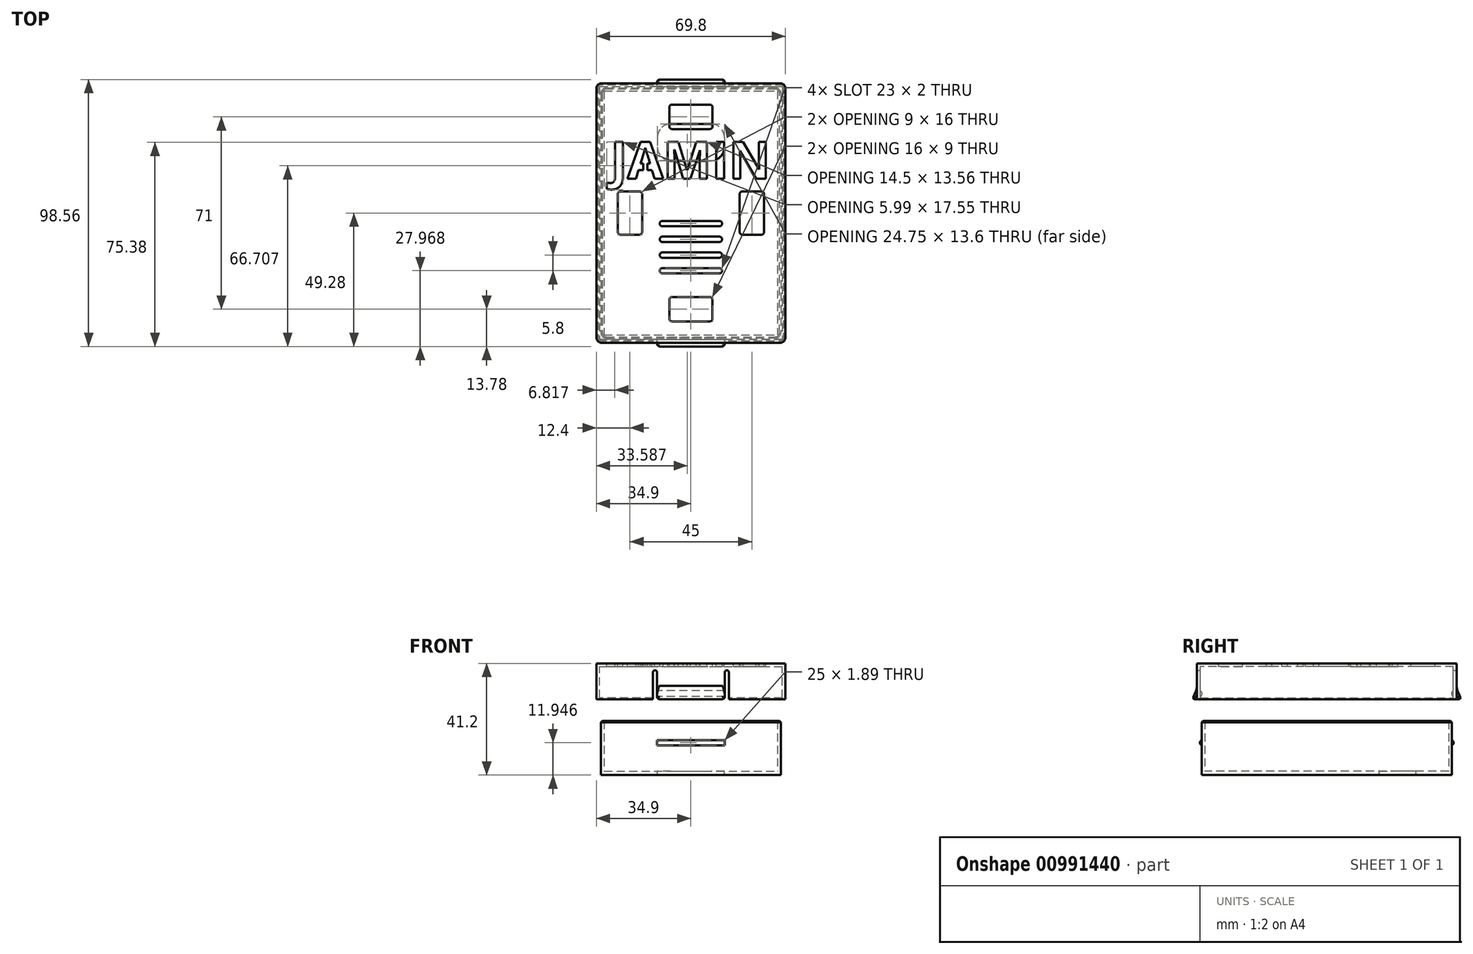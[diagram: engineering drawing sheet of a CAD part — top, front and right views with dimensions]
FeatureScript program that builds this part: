
annotation { "Feature Type Name" : "Feature", "Feature Type Description" : "" }
export const myFeature = defineFeature(function(context is Context, id is Id, definition is map)
    precondition{}
    {
        {
            var Q0;
            Q0=qCreatedBy(makeId("Top.planeOp"),FACE);
            var sketch = newSketch(context, id + "F0", { "sketchPlane" : qUnion([Q0])});
            skLineSegment(sketch, "E0.bottom", {"start": v(-32, 45) * mm, "end": v(32, 45) * mm});
            skLineSegment(sketch, "E0.top", {"start": v(-32, -45) * mm, "end": v(32, -45) * mm});
            skLineSegment(sketch, "E0.left", {"start": v(-32, 45) * mm, "end": v(-32, -45) * mm});
            skLineSegment(sketch, "E0.right", {"start": v(32, 45) * mm, "end": v(32, -45) * mm});
            skLineSegment(sketch, "E1.0", {"start": v(-33.2, 46.2) * mm, "end": v(-33.2, -46.2) * mm});
            skLineSegment(sketch, "E1.1", {"start": v(-33.2, 46.2) * mm, "end": v(33.2, 46.2) * mm});
            skLineSegment(sketch, "E1.2", {"start": v(33.2, 46.2) * mm, "end": v(33.2, -46.2) * mm});
            skLineSegment(sketch, "E1.3", {"start": v(-33.2, -46.2) * mm, "end": v(33.2, -46.2) * mm});
            skSolve(sketch);
        }
        {
            var Q0;
            Q0=makeQuery(id+"F0.imprint","IMPRINT",FACE,{"disambiguationData":[TD([[makeQuery(id+"F0.imprint","IMPRINT",EDGE,{"derivedFrom":sQuery(id+"F0.wireOp",EDGE,"E0.bottom")}),-1.0]])]});
            extrude(context, id + "F1", {"entities" : qUnion([Q0]), "depth" : 1.4 * mm, "offsetDistance" : 25 * mm});
        }
        {
            var Q0;
            Q0=makeQuery(id+"F0.imprint","IMPRINT",FACE,{"disambiguationData":[TD([[makeQuery(id+"F0.imprint","IMPRINT",EDGE,{"derivedFrom":sQuery(id+"F0.wireOp",EDGE,"E0.bottom")}),1.0]])]});
            extrude(context, id + "F2", {"entities" : qUnion([Q0]), "operationType" : NewBodyOperationType.ADD, "depth" : 20 * mm, "offsetDistance" : 25 * mm});
        }
        {
            var Q0;
            Q0=makeQuery(id+"F1.opExtrude","CAP_FACE",FACE,{"disambiguationData":[OSD([sQuery(id+"F0.wireOp",EDGE,"E0.bottom"),sQuery(id+"F0.wireOp",EDGE,"E0.top"),sQuery(id+"F0.wireOp",EDGE,"E0.left"),sQuery(id+"F0.wireOp",EDGE,"E0.right")])],"isStart":false});
            var sketch = newSketch(context, id + "F3", { "sketchPlane" : qUnion([Q0])});
            skLineSegment(sketch, "E2.bottom", {"start": v(-12.38, 32.9) * mm, "end": v(12.38, 32.9) * mm});
            skLineSegment(sketch, "E2.top", {"start": v(-12.38, 19.3) * mm, "end": v(12.38, 19.3) * mm});
            skLineSegment(sketch, "E2.left", {"start": v(-12.38, 32.9) * mm, "end": v(-12.38, 19.3) * mm});
            skLineSegment(sketch, "E2.right", {"start": v(12.38, 32.9) * mm, "end": v(12.38, 19.3) * mm});
            skSolve(sketch);
        }
        {
            var Q0;
            Q0=makeQuery(id+"F3.imprint","IMPRINT",FACE,{"disambiguationData":[TD([[makeQuery(id+"F3.imprint","IMPRINT",EDGE,{"derivedFrom":sQuery(id+"F3.wireOp",EDGE,"E2.bottom")}),-1.0]])]});
            extrude(context, id + "F4", {"entities" : qUnion([Q0]), "operationType" : NewBodyOperationType.REMOVE, "oppositeDirection" : true, "depth" : 25 * mm, "offsetDistance" : 25 * mm});
        }
        {
            var Q0;
            Q0=makeQuery(id+"F4.boolean.opBoolean","COPY",EDGE,{"derivedFrom":makeQuery(id+"F4.opExtrude","SWEPT_EDGE",EDGE,{"disambiguationData":[OSD([sQuery(id+"F3.wireOp",EDGE,"E2.bottom"),sQuery(id+"F3.wireOp",EDGE,"E2.left")])]})});
            var Q1;
            Q1=makeQuery(id+"F4.boolean.opBoolean","COPY",EDGE,{"derivedFrom":makeQuery(id+"F4.opExtrude","SWEPT_EDGE",EDGE,{"disambiguationData":[OSD([sQuery(id+"F3.wireOp",EDGE,"E2.top"),sQuery(id+"F3.wireOp",EDGE,"E2.right")])]})});
            var Q2;
            Q2=makeQuery(id+"F4.boolean.opBoolean","COPY",EDGE,{"derivedFrom":makeQuery(id+"F4.opExtrude","SWEPT_EDGE",EDGE,{"disambiguationData":[OSD([sQuery(id+"F3.wireOp",EDGE,"E2.bottom"),sQuery(id+"F3.wireOp",EDGE,"E2.right")])]})});
            var Q3;
            Q3=makeQuery(id+"F4.boolean.opBoolean","COPY",EDGE,{"derivedFrom":makeQuery(id+"F4.opExtrude","SWEPT_EDGE",EDGE,{"disambiguationData":[OSD([sQuery(id+"F3.wireOp",EDGE,"E2.top"),sQuery(id+"F3.wireOp",EDGE,"E2.left")])]})});
            fillet(context, id + "F5", {"entities" : qUnion([Q0, Q1, Q2, Q3]), "radius" : 5 * mm, "tangentPropagation" : true, "allowEdgeOverflow" : false});
        }
        {
            var Q0;
            Q0=makeQuery(id+"F2.opExtrude","SWEPT_EDGE",EDGE,{"disambiguationData":[OSD([sQuery(id+"F0.wireOp",EDGE,"E1.2"),sQuery(id+"F0.wireOp",EDGE,"E1.3")])]});
            var Q1;
            Q1=makeQuery(id+"F2.opExtrude","SWEPT_EDGE",EDGE,{"disambiguationData":[OSD([sQuery(id+"F0.wireOp",EDGE,"E1.1"),sQuery(id+"F0.wireOp",EDGE,"E1.2")])]});
            var Q2;
            Q2=makeQuery(id+"F2.opExtrude","SWEPT_EDGE",EDGE,{"disambiguationData":[OSD([sQuery(id+"F0.wireOp",EDGE,"E1.0"),sQuery(id+"F0.wireOp",EDGE,"E1.1")])]});
            var Q3;
            Q3=makeQuery(id+"F2.opExtrude","SWEPT_EDGE",EDGE,{"disambiguationData":[OSD([sQuery(id+"F0.wireOp",EDGE,"E1.0"),sQuery(id+"F0.wireOp",EDGE,"E1.3")])]});
            fillet(context, id + "F6", {"entities" : qUnion([Q0, Q1, Q2, Q3]), "radius" : 2 * mm, "tangentPropagation" : true, "allowEdgeOverflow" : false});
        }
        {
            var Q0;
            Q0=qCreatedBy(makeId("Right.planeOp"),FACE);
            var sketch = newSketch(context, id + "F7", { "sketchPlane" : qUnion([Q0])});
            skArc(sketch, "E3", {"start": v(-46.2, 12.9) * mm, "mid": v(-46.81, 11.95) * mm, "end": v(-46.2, 11) * mm});
            skLineSegment(sketch, "E4", {"start": v(-46.2, 12.9) * mm, "end": v(-46.2, 11) * mm});
            skSolve(sketch);
        }
        {
            var Q0;
            Q0=makeQuery(id+"F7.imprint","IMPRINT",FACE,{"disambiguationData":[TD([[makeQuery(id+"F7.imprint","IMPRINT",EDGE,{"derivedFrom":sQuery(id+"F7.wireOp",EDGE,"E3")}),1.0]])]});
            extrude(context, id + "F8", {"entities" : qUnion([Q0]), "endBound" : BoundingType.SYMMETRIC, "depth" : 25 * mm, "offsetDistance" : 25 * mm});
        }
        {
            var Q0;
            Q0=makeQuery(id+"F8.opExtrude","SWEPT_BODY",BODY,{"disambiguationData":[OSD([sQuery(id+"F7.wireOp",EDGE,"E3"),sQuery(id+"F7.wireOp",EDGE,"E4")])]});
            var Q1;
            Q1=qCreatedBy(makeId("Front.planeOp"),FACE);
            mirror(context, id + "F9", {"operationType" : NewBodyOperationType.ADD, "entities" : qUnion([Q0]), "mirrorPlane" : qUnion([Q1])});
        }
        {
            var Q0;
            Q0=qCreatedBy(makeId("Top.planeOp"),FACE);
            cPlane(context, id + "F10", {"entities" : qUnion([Q0]), "cplaneType" : CPlaneType.OFFSET, "offset" : 40 * mm, "width" : 150 * mm, "height" : 150 * mm});
        }
        {
            var Q0;
            Q0=qCreatedBy(id+"F10.planeOp",FACE);
            var sketch = newSketch(context, id + "F11", { "sketchPlane" : qUnion([Q0])});
            skLineSegment(sketch, "E5.bottom", {"start": v(-33.7, 46.7) * mm, "end": v(33.7, 46.7) * mm});
            skLineSegment(sketch, "E5.top", {"start": v(-33.7, -46.7) * mm, "end": v(33.7, -46.7) * mm});
            skLineSegment(sketch, "E5.left", {"start": v(-33.7, 46.7) * mm, "end": v(-33.7, -46.7) * mm});
            skLineSegment(sketch, "E5.right", {"start": v(33.7, 46.7) * mm, "end": v(33.7, -46.7) * mm});
            skLineSegment(sketch, "E6.0", {"start": v(-34.9, 47.9) * mm, "end": v(-34.9, -47.9) * mm});
            skLineSegment(sketch, "E6.1", {"start": v(-34.9, 47.9) * mm, "end": v(34.9, 47.9) * mm});
            skLineSegment(sketch, "E6.2", {"start": v(34.9, 47.9) * mm, "end": v(34.9, -47.9) * mm});
            skLineSegment(sketch, "E6.3", {"start": v(-34.9, -47.9) * mm, "end": v(34.9, -47.9) * mm});
            skSolve(sketch);
        }
        {
            var Q0;
            Q0=makeQuery(id+"F11.imprint","IMPRINT",FACE,{"disambiguationData":[TD([[makeQuery(id+"F11.imprint","IMPRINT",EDGE,{"derivedFrom":sQuery(id+"F11.wireOp",EDGE,"E5.bottom")}),1.0]])]});
            extrude(context, id + "F12", {"entities" : qUnion([Q0]), "operationType" : NewBodyOperationType.ADD, "oppositeDirection" : true, "depth" : 12 * mm, "offsetDistance" : 25 * mm});
        }
        {
            var Q0;
            Q0=qCreatedBy(makeId("Right.planeOp"),FACE);
            var sketch = newSketch(context, id + "F13", { "sketchPlane" : qUnion([Q0])});
            skArc(sketch, "E7", {"start": v(46.7, 31.15) * mm, "mid": v(46.03, 30.07) * mm, "end": v(46.7, 29) * mm});
            skLineSegment(sketch, "E8", {"start": v(46.7, 31.15) * mm, "end": v(46.7, 29) * mm});
            skSolve(sketch);
        }
        {
            var Q0;
            Q0=makeQuery(id+"F13.imprint","IMPRINT",FACE,{"disambiguationData":[TD([[makeQuery(id+"F13.imprint","IMPRINT",EDGE,{"derivedFrom":sQuery(id+"F13.wireOp",EDGE,"E7")}),1.0]])]});
            extrude(context, id + "F14", {"entities" : qUnion([Q0]), "endBound" : BoundingType.SYMMETRIC, "depth" : 25 * mm, "offsetDistance" : 25 * mm});
        }
        {
            var Q0;
            Q0=makeQuery(id+"F14.opExtrude","SWEPT_BODY",BODY,{"disambiguationData":[OSD([sQuery(id+"F13.wireOp",EDGE,"E7"),sQuery(id+"F13.wireOp",EDGE,"E8")])]});
            var Q1;
            Q1=qCreatedBy(makeId("Front.planeOp"),FACE);
            mirror(context, id + "F15", {"operationType" : NewBodyOperationType.ADD, "entities" : qUnion([Q0]), "mirrorPlane" : qUnion([Q1])});
        }
        {
            var Q0;
            Q0=makeQuery(id+"F12.opExtrude","CAP_FACE",FACE,{"disambiguationData":[OSD([sQuery(id+"F11.wireOp",EDGE,"E5.bottom"),sQuery(id+"F11.wireOp",EDGE,"E5.top"),sQuery(id+"F11.wireOp",EDGE,"E5.left"),sQuery(id+"F11.wireOp",EDGE,"E5.right"),sQuery(id+"F11.wireOp",EDGE,"E6.0"),sQuery(id+"F11.wireOp",EDGE,"E6.1"),sQuery(id+"F11.wireOp",EDGE,"E6.2"),sQuery(id+"F11.wireOp",EDGE,"E6.3")])],"isStart":true});
            var sketch = newSketch(context, id + "F16", { "sketchPlane" : qUnion([Q0])});
            skLineSegment(sketch, "E9.bottom", {"start": v(-34.9, 47.9) * mm, "end": v(34.9, 47.9) * mm});
            skLineSegment(sketch, "E9.top", {"start": v(-34.9, -47.9) * mm, "end": v(34.9, -47.9) * mm});
            skLineSegment(sketch, "E9.left", {"start": v(-34.9, 47.9) * mm, "end": v(-34.9, -47.9) * mm});
            skLineSegment(sketch, "E9.right", {"start": v(34.9, 47.9) * mm, "end": v(34.9, -47.9) * mm});
            skSolve(sketch);
        }
        {
            var Q0;
            Q0 = qSketchRegion(id + "F16", true);
            extrude(context, id + "F17", {"entities" : qUnion([Q0]), "operationType" : NewBodyOperationType.ADD, "depth" : 1.2 * mm, "offsetDistance" : 25 * mm});
        }
        {
            var Q0;
            Q0=makeQuery(id+"F17.boolean.opBoolean","MERGE",EDGE,{"derivedFrom":[makeQuery(id+"F12.opExtrude","SWEPT_EDGE",EDGE,{"disambiguationData":[OSD([sQuery(id+"F11.wireOp",EDGE,"E6.1"),sQuery(id+"F11.wireOp",EDGE,"E6.2")])]}),makeQuery(id+"F17.opExtrude","SWEPT_EDGE",EDGE,{"disambiguationData":[OSD([sQuery(id+"F16.wireOp",EDGE,"E9.bottom"),sQuery(id+"F16.wireOp",EDGE,"E9.right")])]})]});
            var Q1;
            Q1=makeQuery(id+"F17.boolean.opBoolean","MERGE",EDGE,{"derivedFrom":[makeQuery(id+"F12.opExtrude","SWEPT_EDGE",EDGE,{"disambiguationData":[OSD([sQuery(id+"F11.wireOp",EDGE,"E6.0"),sQuery(id+"F11.wireOp",EDGE,"E6.1")])]}),makeQuery(id+"F17.opExtrude","SWEPT_EDGE",EDGE,{"disambiguationData":[OSD([sQuery(id+"F16.wireOp",EDGE,"E9.bottom"),sQuery(id+"F16.wireOp",EDGE,"E9.left")])]})]});
            var Q2;
            Q2=makeQuery(id+"F17.boolean.opBoolean","MERGE",EDGE,{"derivedFrom":[makeQuery(id+"F12.opExtrude","SWEPT_EDGE",EDGE,{"disambiguationData":[OSD([sQuery(id+"F11.wireOp",EDGE,"E6.0"),sQuery(id+"F11.wireOp",EDGE,"E6.3")])]}),makeQuery(id+"F17.opExtrude","SWEPT_EDGE",EDGE,{"disambiguationData":[OSD([sQuery(id+"F16.wireOp",EDGE,"E9.top"),sQuery(id+"F16.wireOp",EDGE,"E9.left")])]})]});
            var Q3;
            Q3=makeQuery(id+"F17.boolean.opBoolean","MERGE",EDGE,{"derivedFrom":[makeQuery(id+"F12.opExtrude","SWEPT_EDGE",EDGE,{"disambiguationData":[OSD([sQuery(id+"F11.wireOp",EDGE,"E6.2"),sQuery(id+"F11.wireOp",EDGE,"E6.3")])]}),makeQuery(id+"F17.opExtrude","SWEPT_EDGE",EDGE,{"disambiguationData":[OSD([sQuery(id+"F16.wireOp",EDGE,"E9.top"),sQuery(id+"F16.wireOp",EDGE,"E9.right")])]})]});
            fillet(context, id + "F18", {"entities" : qUnion([Q0, Q1, Q2, Q3]), "radius" : 2 * mm, "tangentPropagation" : true, "allowEdgeOverflow" : false});
        }
        {
            var Q0;
            Q0=qCreatedBy(makeId("Front.planeOp"),FACE);
            var sketch = newSketch(context, id + "F19", { "sketchPlane" : qUnion([Q0])});
            skLineSegment(sketch, "E10.bottom", {"start": v(12.5, 23.7) * mm, "end": v(14, 23.7) * mm});
            skLineSegment(sketch, "E10.top", {"start": v(12.5, 38.7) * mm, "end": v(14, 38.7) * mm});
            skLineSegment(sketch, "E10.left", {"start": v(12.5, 23.7) * mm, "end": v(12.5, 38.7) * mm});
            skLineSegment(sketch, "E10.right", {"start": v(14, 23.7) * mm, "end": v(14, 38.7) * mm});
            skLineSegment(sketch, "E11.MirrorCS", {"start": v(-12.5, 23.7) * mm, "end": v(-12.5, 38.7) * mm});
            skLineSegment(sketch, "E12.MirrorCS", {"start": v(-14, 23.7) * mm, "end": v(-14, 38.7) * mm});
            skLineSegment(sketch, "E13.MirrorCS", {"start": v(-12.5, 38.7) * mm, "end": v(-14, 38.7) * mm});
            skLineSegment(sketch, "E14.MirrorCS", {"start": v(-12.5, 23.7) * mm, "end": v(-14, 23.7) * mm});
            skSolve(sketch);
        }
        {
            var Q0;
            Q0=makeQuery(id+"F19.imprint","IMPRINT",FACE,{"disambiguationData":[TD([[makeQuery(id+"F19.imprint","IMPRINT",EDGE,{"derivedFrom":sQuery(id+"F19.wireOp",EDGE,"E10.bottom")}),1.0]])]});
            var Q1;
            Q1=makeQuery(id+"F19.imprint","IMPRINT",FACE,{"disambiguationData":[TD([[makeQuery(id+"F19.imprint","IMPRINT",EDGE,{"derivedFrom":sQuery(id+"F19.wireOp",EDGE,"E11.MirrorCS")}),1.0]])]});
            extrude(context, id + "F20", {"entities" : qUnion([Q0, Q1]), "operationType" : NewBodyOperationType.REMOVE, "endBound" : BoundingType.SYMMETRIC, "oppositeDirection" : true, "depth" : 200 * mm, "offsetDistance" : 25 * mm});
        }
        {
            var Q0;
            Q0=qCreatedBy(makeId("Right.planeOp"),FACE);
            var sketch = newSketch(context, id + "F21", { "sketchPlane" : qUnion([Q0])});
            skFitSpline(sketch, "E15", {"points": [v(47.9, 32.98) * mm, v(48.43, 30.67) * mm, v(49.27, 28.33) * mm, v(47.9, 28) * mm], "startDerivative": vector(1.04, -7.9) * mm, "endDerivative": vector(-8.37, 0.03) * mm});
            skLineSegment(sketch, "E16", {"start": v(47.9, 32.98) * mm, "end": v(47.9, 28) * mm});
            skSolve(sketch);
        }
        {
            var Q0;
            Q0=makeQuery(id+"F21.imprint","IMPRINT",FACE,{"disambiguationData":[TD([[makeQuery(id+"F21.imprint","IMPRINT",EDGE,{"derivedFrom":sQuery(id+"F21.wireOp",EDGE,"E15")}),-1.0]])]});
            extrude(context, id + "F22", {"entities" : qUnion([Q0]), "endBound" : BoundingType.SYMMETRIC, "depth" : 25 * mm, "offsetDistance" : 25 * mm});
        }
        {
            var Q0;
            {var subQ0=sQuery(id+"F19.wireOp",EDGE,"E10.top");var subQ1=sQuery(id+"F19.wireOp",EDGE,"E10.left");Q0=makeQuery(id+"F20.boolean.opBoolean","COPY",EDGE,{"disambiguationData":[topologyDisambiguationEdgeConnected([makeQuery(id+"F14.opExtrude","CAP_FACE",FACE,{"disambiguationData":[OSD([sQuery(id+"F13.wireOp",EDGE,"E7"),sQuery(id+"F13.wireOp",EDGE,"E8")])],"isStart":false})])],"derivedFrom":makeQuery(id+"F20.opExtrude","SWEPT_EDGE",EDGE,{"disambiguationData":[OSD([subQ0,subQ1])]})});}
            var Q1;
            {var subQ0=sQuery(id+"F19.wireOp",EDGE,"E10.right");var subQ1=sQuery(id+"F19.wireOp",EDGE,"E10.top");Q1=makeQuery(id+"F20.boolean.opBoolean","COPY",EDGE,{"disambiguationData":[TD([makeQuery(id+"F12.opExtrude","SWEPT_FACE",FACE,{"disambiguationData":[OSD([sQuery(id+"F11.wireOp",EDGE,"E5.bottom")])]})])],"derivedFrom":makeQuery(id+"F20.opExtrude","SWEPT_EDGE",EDGE,{"disambiguationData":[OSD([subQ1,subQ0])]})});}
            var Q2;
            {var subQ0=sQuery(id+"F19.wireOp",EDGE,"E11.MirrorCS");var subQ1=sQuery(id+"F19.wireOp",EDGE,"E13.MirrorCS");Q2=makeQuery(id+"F20.boolean.opBoolean","COPY",EDGE,{"disambiguationData":[topologyDisambiguationEdgeConnected([makeQuery(id+"F14.opExtrude","CAP_FACE",FACE,{"disambiguationData":[OSD([sQuery(id+"F13.wireOp",EDGE,"E7"),sQuery(id+"F13.wireOp",EDGE,"E8")])],"isStart":true})])],"derivedFrom":makeQuery(id+"F20.opExtrude","SWEPT_EDGE",EDGE,{"disambiguationData":[OSD([subQ0,subQ1])]})});}
            var Q3;
            {var subQ0=sQuery(id+"F19.wireOp",EDGE,"E12.MirrorCS");var subQ1=sQuery(id+"F19.wireOp",EDGE,"E13.MirrorCS");Q3=makeQuery(id+"F20.boolean.opBoolean","COPY",EDGE,{"disambiguationData":[TD([makeQuery(id+"F12.opExtrude","SWEPT_FACE",FACE,{"disambiguationData":[OSD([sQuery(id+"F11.wireOp",EDGE,"E5.bottom")])]})])],"derivedFrom":makeQuery(id+"F20.opExtrude","SWEPT_EDGE",EDGE,{"disambiguationData":[OSD([subQ0,subQ1])]})});}
            var Q4;
            {var subQ0=sQuery(id+"F19.wireOp",EDGE,"E10.top");var subQ1=sQuery(id+"F19.wireOp",EDGE,"E10.left");Q4=makeQuery(id+"F20.boolean.opBoolean","COPY",EDGE,{"disambiguationData":[topologyDisambiguationEdgeConnected([makeQuery(id+"F15.opPattern","COPY",FACE,{"derivedFrom":makeQuery(id+"F14.opExtrude","CAP_FACE",FACE,{"disambiguationData":[OSD([sQuery(id+"F13.wireOp",EDGE,"E7"),sQuery(id+"F13.wireOp",EDGE,"E8")])],"isStart":false}),"instanceName":"1"})])],"derivedFrom":makeQuery(id+"F20.opExtrude","SWEPT_EDGE",EDGE,{"disambiguationData":[OSD([subQ0,subQ1])]})});}
            var Q5;
            {var subQ0=sQuery(id+"F19.wireOp",EDGE,"E12.MirrorCS");var subQ1=sQuery(id+"F19.wireOp",EDGE,"E13.MirrorCS");Q5=makeQuery(id+"F20.boolean.opBoolean","COPY",EDGE,{"disambiguationData":[TD([makeQuery(id+"F12.opExtrude","SWEPT_FACE",FACE,{"disambiguationData":[OSD([sQuery(id+"F11.wireOp",EDGE,"E5.top")])]})])],"derivedFrom":makeQuery(id+"F20.opExtrude","SWEPT_EDGE",EDGE,{"disambiguationData":[OSD([subQ0,subQ1])]})});}
            var Q6;
            {var subQ0=sQuery(id+"F19.wireOp",EDGE,"E11.MirrorCS");var subQ1=sQuery(id+"F19.wireOp",EDGE,"E13.MirrorCS");Q6=makeQuery(id+"F20.boolean.opBoolean","COPY",EDGE,{"disambiguationData":[topologyDisambiguationEdgeConnected([makeQuery(id+"F15.opPattern","COPY",FACE,{"derivedFrom":makeQuery(id+"F14.opExtrude","CAP_FACE",FACE,{"disambiguationData":[OSD([sQuery(id+"F13.wireOp",EDGE,"E7"),sQuery(id+"F13.wireOp",EDGE,"E8")])],"isStart":true}),"instanceName":"1"})])],"derivedFrom":makeQuery(id+"F20.opExtrude","SWEPT_EDGE",EDGE,{"disambiguationData":[OSD([subQ0,subQ1])]})});}
            var Q7;
            {var subQ0=sQuery(id+"F19.wireOp",EDGE,"E10.top");var subQ1=sQuery(id+"F19.wireOp",EDGE,"E10.right");Q7=makeQuery(id+"F20.boolean.opBoolean","COPY",EDGE,{"disambiguationData":[TD([makeQuery(id+"F12.opExtrude","SWEPT_FACE",FACE,{"disambiguationData":[OSD([sQuery(id+"F11.wireOp",EDGE,"E5.top")])]})])],"derivedFrom":makeQuery(id+"F20.opExtrude","SWEPT_EDGE",EDGE,{"disambiguationData":[OSD([subQ0,subQ1])]})});}
            fillet(context, id + "F23", {"entities" : qUnion([Q0, Q1, Q2, Q3, Q4, Q5, Q6, Q7]), "radius" : 0.75 * mm, "tangentPropagation" : true, "allowEdgeOverflow" : false});
        }
        {
            var Q0;
            Q0=makeQuery(id+"F22.opExtrude","SWEPT_BODY",BODY,{"disambiguationData":[OSD([sQuery(id+"F21.wireOp",EDGE,"E15"),sQuery(id+"F21.wireOp",EDGE,"E16")])]});
            var Q1;
            Q1=qCreatedBy(makeId("Front.planeOp"),FACE);
            mirror(context, id + "F24", {"operationType" : NewBodyOperationType.ADD, "entities" : qUnion([Q0]), "mirrorPlane" : qUnion([Q1])});
        }
        {
            var Q0;
            {var subQ0=makeQuery(id+"F12.opExtrude","CAP_FACE",FACE,{"disambiguationData":[OSD([sQuery(id+"F11.wireOp",EDGE,"E5.bottom"),sQuery(id+"F11.wireOp",EDGE,"E5.top"),sQuery(id+"F11.wireOp",EDGE,"E5.left"),sQuery(id+"F11.wireOp",EDGE,"E5.right"),sQuery(id+"F11.wireOp",EDGE,"E6.0"),sQuery(id+"F11.wireOp",EDGE,"E6.1"),sQuery(id+"F11.wireOp",EDGE,"E6.2"),sQuery(id+"F11.wireOp",EDGE,"E6.3")])],"isStart":false});var subQ1=makeQuery(id+"F20.opExtrude","SWEPT_FACE",FACE,{"disambiguationData":[OSD([sQuery(id+"F19.wireOp",EDGE,"E11.MirrorCS")])]});Q0=makeQuery(id+"F20.boolean.opBoolean","INTERSECT",EDGE,{"disambiguationData":[topologyDisambiguationEdgeConnected([makeQuery(id+"F14.opExtrude","CAP_FACE",FACE,{"disambiguationData":[OSD([sQuery(id+"F13.wireOp",EDGE,"E7"),sQuery(id+"F13.wireOp",EDGE,"E8")])],"isStart":true})])],"derivedFrom":[subQ0,subQ1]});}
            var Q1;
            {var subQ0=makeQuery(id+"F12.opExtrude","CAP_FACE",FACE,{"disambiguationData":[OSD([sQuery(id+"F11.wireOp",EDGE,"E5.bottom"),sQuery(id+"F11.wireOp",EDGE,"E5.top"),sQuery(id+"F11.wireOp",EDGE,"E5.left"),sQuery(id+"F11.wireOp",EDGE,"E5.right"),sQuery(id+"F11.wireOp",EDGE,"E6.0"),sQuery(id+"F11.wireOp",EDGE,"E6.1"),sQuery(id+"F11.wireOp",EDGE,"E6.2"),sQuery(id+"F11.wireOp",EDGE,"E6.3")])],"isStart":false});var subQ1=makeQuery(id+"F20.opExtrude","SWEPT_FACE",FACE,{"disambiguationData":[OSD([sQuery(id+"F19.wireOp",EDGE,"E10.left")])]});Q1=makeQuery(id+"F20.boolean.opBoolean","INTERSECT",EDGE,{"disambiguationData":[topologyDisambiguationEdgeConnected([makeQuery(id+"F14.opExtrude","CAP_FACE",FACE,{"disambiguationData":[OSD([sQuery(id+"F13.wireOp",EDGE,"E7"),sQuery(id+"F13.wireOp",EDGE,"E8")])],"isStart":false})])],"derivedFrom":[subQ0,subQ1]});}
            var Q2;
            {var subQ0=makeQuery(id+"F12.opExtrude","CAP_FACE",FACE,{"disambiguationData":[OSD([sQuery(id+"F11.wireOp",EDGE,"E5.bottom"),sQuery(id+"F11.wireOp",EDGE,"E5.top"),sQuery(id+"F11.wireOp",EDGE,"E5.left"),sQuery(id+"F11.wireOp",EDGE,"E5.right"),sQuery(id+"F11.wireOp",EDGE,"E6.0"),sQuery(id+"F11.wireOp",EDGE,"E6.1"),sQuery(id+"F11.wireOp",EDGE,"E6.2"),sQuery(id+"F11.wireOp",EDGE,"E6.3")])],"isStart":false});var subQ1=makeQuery(id+"F20.opExtrude","SWEPT_FACE",FACE,{"disambiguationData":[OSD([sQuery(id+"F19.wireOp",EDGE,"E10.left")])]});Q2=makeQuery(id+"F20.boolean.opBoolean","INTERSECT",EDGE,{"disambiguationData":[topologyDisambiguationEdgeConnected([makeQuery(id+"F15.opPattern","COPY",FACE,{"derivedFrom":makeQuery(id+"F14.opExtrude","CAP_FACE",FACE,{"disambiguationData":[OSD([sQuery(id+"F13.wireOp",EDGE,"E7"),sQuery(id+"F13.wireOp",EDGE,"E8")])],"isStart":false}),"instanceName":"1"})])],"derivedFrom":[subQ0,subQ1]});}
            var Q3;
            {var subQ0=makeQuery(id+"F12.opExtrude","CAP_FACE",FACE,{"disambiguationData":[OSD([sQuery(id+"F11.wireOp",EDGE,"E5.bottom"),sQuery(id+"F11.wireOp",EDGE,"E5.top"),sQuery(id+"F11.wireOp",EDGE,"E5.left"),sQuery(id+"F11.wireOp",EDGE,"E5.right"),sQuery(id+"F11.wireOp",EDGE,"E6.0"),sQuery(id+"F11.wireOp",EDGE,"E6.1"),sQuery(id+"F11.wireOp",EDGE,"E6.2"),sQuery(id+"F11.wireOp",EDGE,"E6.3")])],"isStart":false});var subQ1=makeQuery(id+"F20.opExtrude","SWEPT_FACE",FACE,{"disambiguationData":[OSD([sQuery(id+"F19.wireOp",EDGE,"E11.MirrorCS")])]});Q3=makeQuery(id+"F20.boolean.opBoolean","INTERSECT",EDGE,{"disambiguationData":[topologyDisambiguationEdgeConnected([makeQuery(id+"F15.opPattern","COPY",FACE,{"derivedFrom":makeQuery(id+"F14.opExtrude","CAP_FACE",FACE,{"disambiguationData":[OSD([sQuery(id+"F13.wireOp",EDGE,"E7"),sQuery(id+"F13.wireOp",EDGE,"E8")])],"isStart":true}),"instanceName":"1"})])],"derivedFrom":[subQ0,subQ1]});}
            fillet(context, id + "F25", {"entities" : qUnion([Q0, Q1, Q2, Q3]), "radius" : 1 * mm, "tangentPropagation" : true, "allowEdgeOverflow" : false});
        }
        {
            var Q0;
            Q0=makeQuery(id+"F17.opExtrude","CAP_FACE",FACE,{"disambiguationData":[OSD([sQuery(id+"F16.wireOp",EDGE,"E9.bottom"),sQuery(id+"F16.wireOp",EDGE,"E9.top"),sQuery(id+"F16.wireOp",EDGE,"E9.left"),sQuery(id+"F16.wireOp",EDGE,"E9.right")])],"isStart":false});
            var sketch = newSketch(context, id + "F26", { "sketchPlane" : qUnion([Q0])});
            skLineSegment(sketch, "E17.bottom", {"start": v(-8, 40) * mm, "end": v(8, 40) * mm});
            skLineSegment(sketch, "E17.top", {"start": v(-8, 31) * mm, "end": v(8, 31) * mm});
            skLineSegment(sketch, "E17.left", {"start": v(-8, 40) * mm, "end": v(-8, 31) * mm});
            skLineSegment(sketch, "E17.right", {"start": v(8, 40) * mm, "end": v(8, 31) * mm});
            skLineSegment(sketch, "E18.MirrorCS", {"start": v(-8, -40) * mm, "end": v(-8, -31) * mm});
            skLineSegment(sketch, "E19.MirrorCS", {"start": v(-8, -40) * mm, "end": v(8, -40) * mm});
            skLineSegment(sketch, "E20.MirrorCS", {"start": v(8, -40) * mm, "end": v(8, -31) * mm});
            skLineSegment(sketch, "E21.MirrorCS", {"start": v(-8, -31) * mm, "end": v(8, -31) * mm});
            skLineSegment(sketch, "E22.bottom", {"start": v(-27, 8) * mm, "end": v(-18, 8) * mm});
            skLineSegment(sketch, "E22.top", {"start": v(-27, -8) * mm, "end": v(-18, -8) * mm});
            skLineSegment(sketch, "E22.left", {"start": v(-27, 8) * mm, "end": v(-27, -8) * mm});
            skLineSegment(sketch, "E22.right", {"start": v(-18, 8) * mm, "end": v(-18, -8) * mm});
            skLineSegment(sketch, "E23.MirrorCS", {"start": v(18, 8) * mm, "end": v(18, -8) * mm});
            skLineSegment(sketch, "E24.MirrorCS", {"start": v(27, 8) * mm, "end": v(18, 8) * mm});
            skLineSegment(sketch, "E25.MirrorCS", {"start": v(27, 8) * mm, "end": v(27, -8) * mm});
            skLineSegment(sketch, "E26.MirrorCS", {"start": v(27, -8) * mm, "end": v(18, -8) * mm});
            skSolve(sketch);
        }
        {
            var Q0;
            Q0=makeQuery(id+"F26.imprint","IMPRINT",FACE,{"disambiguationData":[TD([[makeQuery(id+"F26.imprint","IMPRINT",EDGE,{"derivedFrom":sQuery(id+"F26.wireOp",EDGE,"E22.bottom")}),-1.0]])]});
            var Q1;
            Q1=makeQuery(id+"F26.imprint","IMPRINT",FACE,{"disambiguationData":[TD([[makeQuery(id+"F26.imprint","IMPRINT",EDGE,{"derivedFrom":sQuery(id+"F26.wireOp",EDGE,"E17.bottom")}),-1.0]])]});
            var Q2;
            Q2=makeQuery(id+"F26.imprint","IMPRINT",FACE,{"disambiguationData":[TD([[makeQuery(id+"F26.imprint","IMPRINT",EDGE,{"derivedFrom":sQuery(id+"F26.wireOp",EDGE,"E23.MirrorCS")}),1.0]])]});
            var Q3;
            Q3=makeQuery(id+"F26.imprint","IMPRINT",FACE,{"disambiguationData":[TD([[makeQuery(id+"F26.imprint","IMPRINT",EDGE,{"derivedFrom":sQuery(id+"F26.wireOp",EDGE,"E18.MirrorCS")}),-1.0]])]});
            extrude(context, id + "F27", {"entities" : qUnion([Q0, Q1, Q2, Q3]), "operationType" : NewBodyOperationType.REMOVE, "oppositeDirection" : true, "depth" : 4 * mm, "offsetDistance" : 25 * mm});
        }
        {
            var Q0;
            Q0=makeQuery(id+"F17.opExtrude","CAP_FACE",FACE,{"disambiguationData":[OSD([sQuery(id+"F16.wireOp",EDGE,"E9.bottom"),sQuery(id+"F16.wireOp",EDGE,"E9.top"),sQuery(id+"F16.wireOp",EDGE,"E9.left"),sQuery(id+"F16.wireOp",EDGE,"E9.right")])],"isStart":false});
            var sketch = newSketch(context, id + "F28", { "sketchPlane" : qUnion([Q0])});
            skText(sketch, "E27", { "text": "JAMIN", "fontName": "OpenSans-Bold.ttf"});
            const initialGuessF28  = {"E27": [-0.02967, 0.01264, 1, 0, 0.01368]};
            skSetInitialGuess(sketch, initialGuessF28);
            skSolve(sketch);
        }
        {
            var Q0;
            Q0 = qSketchRegion(id + "F28", true);
            extrude(context, id + "F29", {"entities" : qUnion([Q0]), "operationType" : NewBodyOperationType.REMOVE, "oppositeDirection" : true, "depth" : 4 * mm, "offsetDistance" : 25 * mm});
        }
        {
            var Q0;
            Q0=makeQuery(id+"F29.boolean.opBoolean","COPY",FACE,{"derivedFrom":makeQuery(id+"F29.opExtrude","SWEPT_FACE",FACE,{"disambiguationData":[OSD([sQuery(id+"F28.wireOp",EDGE,"E27.sketch_text.stroke-11")])]})});
            var sketch = newSketch(context, id + "F30", { "sketchPlane" : qUnion([Q0])});
            skLineSegment(sketch, "E28.bottom", {"start": v(17.55, 40) * mm, "end": v(16, 40) * mm});
            skLineSegment(sketch, "E28.top", {"start": v(17.55, 41.2) * mm, "end": v(16, 41.2) * mm});
            skLineSegment(sketch, "E28.left", {"start": v(17.55, 40) * mm, "end": v(17.55, 41.2) * mm});
            skLineSegment(sketch, "E28.right", {"start": v(16, 40) * mm, "end": v(16, 41.2) * mm});
            skSolve(sketch);
        }
        {
            var Q0;
            Q0=makeQuery(id+"F30.imprint","IMPRINT",FACE,{"disambiguationData":[TD([[makeQuery(id+"F30.imprint","IMPRINT",EDGE,{"derivedFrom":sQuery(id+"F30.wireOp",EDGE,"E28.bottom")}),1.0]])]});
            var Q1;
            Q1=makeQuery(id+"F29.boolean.opBoolean","COPY",FACE,{"derivedFrom":makeQuery(id+"F29.opExtrude","SWEPT_FACE",FACE,{"disambiguationData":[OSD([sQuery(id+"F28.wireOp",EDGE,"E27.sketch_text.stroke-21")])]})});
            extrude(context, id + "F31", {"entities" : qUnion([Q0]), "endBound" : BoundingType.UP_TO_SURFACE, "depth" : 25 * mm, "endBoundEntityFace" : qUnion([Q1]), "offsetDistance" : 25 * mm});
        }
        {
            var Q0;
            Q0=makeQuery(id+"F29.boolean.opBoolean","SPLIT",BODY,{"disambiguationData":[OD(0.0)],"derivedFrom":makeQuery(id+"F12.opExtrude","SWEPT_BODY",BODY,{"disambiguationData":[OSD([sQuery(id+"F11.wireOp",EDGE,"E5.bottom"),sQuery(id+"F11.wireOp",EDGE,"E5.top"),sQuery(id+"F11.wireOp",EDGE,"E5.left"),sQuery(id+"F11.wireOp",EDGE,"E5.right"),sQuery(id+"F11.wireOp",EDGE,"E6.0"),sQuery(id+"F11.wireOp",EDGE,"E6.1"),sQuery(id+"F11.wireOp",EDGE,"E6.2"),sQuery(id+"F11.wireOp",EDGE,"E6.3")])]})});
            var Q1;
            Q1=makeQuery(id+"F29.boolean.opBoolean","SPLIT",BODY,{"disambiguationData":[OD(1.0)],"derivedFrom":makeQuery(id+"F12.opExtrude","SWEPT_BODY",BODY,{"disambiguationData":[OSD([sQuery(id+"F11.wireOp",EDGE,"E5.bottom"),sQuery(id+"F11.wireOp",EDGE,"E5.top"),sQuery(id+"F11.wireOp",EDGE,"E5.left"),sQuery(id+"F11.wireOp",EDGE,"E5.right"),sQuery(id+"F11.wireOp",EDGE,"E6.0"),sQuery(id+"F11.wireOp",EDGE,"E6.1"),sQuery(id+"F11.wireOp",EDGE,"E6.2"),sQuery(id+"F11.wireOp",EDGE,"E6.3")])]})});
            var Q2;
            Q2=makeQuery(id+"F31.opExtrude","SWEPT_BODY",BODY,{"disambiguationData":[OSD([sQuery(id+"F30.wireOp",EDGE,"E28.bottom"),sQuery(id+"F30.wireOp",EDGE,"E28.top"),sQuery(id+"F30.wireOp",EDGE,"E28.left"),sQuery(id+"F30.wireOp",EDGE,"E28.right")])]});
            booleanBodies(context, id + "F32", {"operationType" : BooleanOperationType.UNION, "tools" : qUnion([Q0, Q1, Q2])});
        }
        {
            var Q0;
            {var subQ0=sQuery(id+"F16.wireOp",EDGE,"E9.right");var subQ1=sQuery(id+"F16.wireOp",EDGE,"E9.left");var subQ2=sQuery(id+"F16.wireOp",EDGE,"E9.top");var subQ3=sQuery(id+"F16.wireOp",EDGE,"E9.bottom");var subQ4=makeQuery(id+"F17.opExtrude","CAP_FACE",FACE,{"disambiguationData":[OSD([subQ3,subQ2,subQ1,subQ0])],"isStart":false});var subQ8=sQuery(id+"F11.wireOp",EDGE,"E6.0");Q0=makeQuery(id+"F32.opBoolean","MERGE",FACE,{"derivedFrom":[makeQuery(id+"F29.boolean.opBoolean","SPLIT",FACE,{"disambiguationData":[TD([makeQuery(id+"F12.opExtrude","SWEPT_FACE",FACE,{"disambiguationData":[OSD([subQ8])]})])],"derivedFrom":subQ4}),makeQuery(id+"F29.boolean.opBoolean","SPLIT",FACE,{"disambiguationData":[TD([makeQuery(id+"F29.opExtrude","SWEPT_FACE",FACE,{"disambiguationData":[OSD([sQuery(id+"F28.wireOp",EDGE,"E27.sketch_text.stroke-18")])]})])],"derivedFrom":subQ4}),makeQuery(id+"F31.opExtrude","SWEPT_FACE",FACE,{"disambiguationData":[OSD([sQuery(id+"F30.wireOp",EDGE,"E28.top")])]})]});}
            var sketch = newSketch(context, id + "F33", { "sketchPlane" : qUnion([Q0])});
            skLineSegment(sketch, "E29.bottom", {"start": v(-11.5, -2.91) * mm, "end": v(11.5, -2.91) * mm});
            skLineSegment(sketch, "E29.top", {"start": v(-11.5, -4.91) * mm, "end": v(11.5, -4.91) * mm});
            skLineSegment(sketch, "E29.left", {"start": v(-11.5, -2.91) * mm, "end": v(-11.5, -4.91) * mm});
            skLineSegment(sketch, "E29.right", {"start": v(11.5, -2.91) * mm, "end": v(11.5, -4.91) * mm});
            skLineSegment(sketch, "E30.0.1.0", {"start": v(-11.5, -8.71) * mm, "end": v(11.5, -8.71) * mm});
            skLineSegment(sketch, "E30.0.1.1", {"start": v(-11.5, -10.71) * mm, "end": v(11.5, -10.71) * mm});
            skLineSegment(sketch, "E30.0.1.2", {"start": v(-11.5, -8.71) * mm, "end": v(-11.5, -10.71) * mm});
            skLineSegment(sketch, "E30.0.1.3", {"start": v(11.5, -8.71) * mm, "end": v(11.5, -10.71) * mm});
            skLineSegment(sketch, "E30.0.2.0", {"start": v(-11.5, -14.51) * mm, "end": v(11.5, -14.51) * mm});
            skLineSegment(sketch, "E30.0.2.1", {"start": v(-11.5, -16.51) * mm, "end": v(11.5, -16.51) * mm});
            skLineSegment(sketch, "E30.0.2.2", {"start": v(-11.5, -14.51) * mm, "end": v(-11.5, -16.51) * mm});
            skLineSegment(sketch, "E30.0.2.3", {"start": v(11.5, -14.51) * mm, "end": v(11.5, -16.51) * mm});
            skLineSegment(sketch, "E30.0.3.0", {"start": v(-11.5, -20.31) * mm, "end": v(11.5, -20.31) * mm});
            skLineSegment(sketch, "E30.0.3.1", {"start": v(-11.5, -22.31) * mm, "end": v(11.5, -22.31) * mm});
            skLineSegment(sketch, "E30.0.3.2", {"start": v(-11.5, -20.31) * mm, "end": v(-11.5, -22.31) * mm});
            skLineSegment(sketch, "E30.0.3.3", {"start": v(11.5, -20.31) * mm, "end": v(11.5, -22.31) * mm});
            skLineSegment(sketch, "E30.direction1", {"start": v(-11.5, -2.91) * mm, "end": v(14.3, -2.91) * mm, "construction": true});
            skLineSegment(sketch, "E30.direction2", {"start": v(-11.5, -2.91) * mm, "end": v(-11.5, -8.71) * mm, "construction": true});
            skSolve(sketch);
        }
        {
            var Q0;
            Q0=makeQuery(id+"F33.imprint","IMPRINT",FACE,{"disambiguationData":[TD([[makeQuery(id+"F33.imprint","IMPRINT",EDGE,{"derivedFrom":sQuery(id+"F33.wireOp",EDGE,"E29.bottom")}),-1.0]])]});
            var Q1;
            Q1=makeQuery(id+"F33.imprint","IMPRINT",FACE,{"disambiguationData":[TD([[makeQuery(id+"F33.imprint","IMPRINT",EDGE,{"derivedFrom":sQuery(id+"F33.wireOp",EDGE,"E30.0.1.0")}),-1.0]])]});
            var Q2;
            Q2=makeQuery(id+"F33.imprint","IMPRINT",FACE,{"disambiguationData":[TD([[makeQuery(id+"F33.imprint","IMPRINT",EDGE,{"derivedFrom":sQuery(id+"F33.wireOp",EDGE,"E30.0.2.0")}),-1.0]])]});
            var Q3;
            Q3=makeQuery(id+"F33.imprint","IMPRINT",FACE,{"disambiguationData":[TD([[makeQuery(id+"F33.imprint","IMPRINT",EDGE,{"derivedFrom":sQuery(id+"F33.wireOp",EDGE,"E30.0.3.0")}),-1.0]])]});
            extrude(context, id + "F34", {"entities" : qUnion([Q0, Q1, Q2, Q3]), "operationType" : NewBodyOperationType.REMOVE, "oppositeDirection" : true, "depth" : 4 * mm, "offsetDistance" : 25 * mm});
        }
        {
            var Q0;
            Q0=makeQuery(id+"F27.boolean.opBoolean","COPY",EDGE,{"derivedFrom":makeQuery(id+"F27.opExtrude","SWEPT_EDGE",EDGE,{"disambiguationData":[OSD([sQuery(id+"F26.wireOp",EDGE,"E17.bottom"),sQuery(id+"F26.wireOp",EDGE,"E17.left")])]})});
            var Q1;
            Q1=makeQuery(id+"F27.boolean.opBoolean","COPY",EDGE,{"derivedFrom":makeQuery(id+"F27.opExtrude","SWEPT_EDGE",EDGE,{"disambiguationData":[OSD([sQuery(id+"F26.wireOp",EDGE,"E17.bottom"),sQuery(id+"F26.wireOp",EDGE,"E17.right")])]})});
            var Q2;
            Q2=makeQuery(id+"F27.boolean.opBoolean","COPY",EDGE,{"derivedFrom":makeQuery(id+"F27.opExtrude","SWEPT_EDGE",EDGE,{"disambiguationData":[OSD([sQuery(id+"F26.wireOp",EDGE,"E17.top"),sQuery(id+"F26.wireOp",EDGE,"E17.right")])]})});
            var Q3;
            Q3=makeQuery(id+"F27.boolean.opBoolean","COPY",EDGE,{"derivedFrom":makeQuery(id+"F27.opExtrude","SWEPT_EDGE",EDGE,{"disambiguationData":[OSD([sQuery(id+"F26.wireOp",EDGE,"E17.top"),sQuery(id+"F26.wireOp",EDGE,"E17.left")])]})});
            var Q4;
            Q4=makeQuery(id+"F34.boolean.opBoolean","COPY",EDGE,{"derivedFrom":makeQuery(id+"F34.opExtrude","SWEPT_EDGE",EDGE,{"disambiguationData":[OSD([sQuery(id+"F33.wireOp",EDGE,"E29.bottom"),sQuery(id+"F33.wireOp",EDGE,"E29.left")])]})});
            var Q5;
            Q5=makeQuery(id+"F27.boolean.opBoolean","COPY",EDGE,{"derivedFrom":makeQuery(id+"F27.opExtrude","SWEPT_EDGE",EDGE,{"disambiguationData":[OSD([sQuery(id+"F26.wireOp",EDGE,"E18.MirrorCS"),sQuery(id+"F26.wireOp",EDGE,"E21.MirrorCS")])]})});
            var Q6;
            Q6=makeQuery(id+"F27.boolean.opBoolean","COPY",EDGE,{"derivedFrom":makeQuery(id+"F27.opExtrude","SWEPT_EDGE",EDGE,{"disambiguationData":[OSD([sQuery(id+"F26.wireOp",EDGE,"E22.bottom"),sQuery(id+"F26.wireOp",EDGE,"E22.left")])]})});
            var Q7;
            Q7=makeQuery(id+"F34.boolean.opBoolean","COPY",EDGE,{"derivedFrom":makeQuery(id+"F34.opExtrude","SWEPT_EDGE",EDGE,{"disambiguationData":[OSD([sQuery(id+"F33.wireOp",EDGE,"E30.0.1.0"),sQuery(id+"F33.wireOp",EDGE,"E30.0.1.2")])]})});
            var Q8;
            Q8=makeQuery(id+"F34.boolean.opBoolean","COPY",EDGE,{"derivedFrom":makeQuery(id+"F34.opExtrude","SWEPT_EDGE",EDGE,{"disambiguationData":[OSD([sQuery(id+"F33.wireOp",EDGE,"E30.0.2.0"),sQuery(id+"F33.wireOp",EDGE,"E30.0.2.2")])]})});
            var Q9;
            Q9=makeQuery(id+"F34.boolean.opBoolean","COPY",EDGE,{"derivedFrom":makeQuery(id+"F34.opExtrude","SWEPT_EDGE",EDGE,{"disambiguationData":[OSD([sQuery(id+"F33.wireOp",EDGE,"E30.0.3.0"),sQuery(id+"F33.wireOp",EDGE,"E30.0.3.2")])]})});
            var Q10;
            Q10=makeQuery(id+"F27.boolean.opBoolean","COPY",EDGE,{"derivedFrom":makeQuery(id+"F27.opExtrude","SWEPT_EDGE",EDGE,{"disambiguationData":[OSD([sQuery(id+"F26.wireOp",EDGE,"E23.MirrorCS"),sQuery(id+"F26.wireOp",EDGE,"E24.MirrorCS")])]})});
            var Q11;
            Q11=makeQuery(id+"F27.boolean.opBoolean","COPY",EDGE,{"derivedFrom":makeQuery(id+"F27.opExtrude","SWEPT_EDGE",EDGE,{"disambiguationData":[OSD([sQuery(id+"F26.wireOp",EDGE,"E24.MirrorCS"),sQuery(id+"F26.wireOp",EDGE,"E25.MirrorCS")])]})});
            var Q12;
            Q12=makeQuery(id+"F34.boolean.opBoolean","COPY",EDGE,{"derivedFrom":makeQuery(id+"F34.opExtrude","SWEPT_EDGE",EDGE,{"disambiguationData":[OSD([sQuery(id+"F33.wireOp",EDGE,"E29.bottom"),sQuery(id+"F33.wireOp",EDGE,"E29.right")])]})});
            var Q13;
            Q13=makeQuery(id+"F34.boolean.opBoolean","COPY",EDGE,{"derivedFrom":makeQuery(id+"F34.opExtrude","SWEPT_EDGE",EDGE,{"disambiguationData":[OSD([sQuery(id+"F33.wireOp",EDGE,"E30.0.1.0"),sQuery(id+"F33.wireOp",EDGE,"E30.0.1.3")])]})});
            var Q14;
            Q14=makeQuery(id+"F34.boolean.opBoolean","COPY",EDGE,{"derivedFrom":makeQuery(id+"F34.opExtrude","SWEPT_EDGE",EDGE,{"disambiguationData":[OSD([sQuery(id+"F33.wireOp",EDGE,"E30.0.2.0"),sQuery(id+"F33.wireOp",EDGE,"E30.0.2.3")])]})});
            var Q15;
            Q15=makeQuery(id+"F34.boolean.opBoolean","COPY",EDGE,{"derivedFrom":makeQuery(id+"F34.opExtrude","SWEPT_EDGE",EDGE,{"disambiguationData":[OSD([sQuery(id+"F33.wireOp",EDGE,"E30.0.3.0"),sQuery(id+"F33.wireOp",EDGE,"E30.0.3.3")])]})});
            var Q16;
            Q16=makeQuery(id+"F27.boolean.opBoolean","COPY",EDGE,{"derivedFrom":makeQuery(id+"F27.opExtrude","SWEPT_EDGE",EDGE,{"disambiguationData":[OSD([sQuery(id+"F26.wireOp",EDGE,"E20.MirrorCS"),sQuery(id+"F26.wireOp",EDGE,"E21.MirrorCS")])]})});
            var Q17;
            Q17=makeQuery(id+"F27.boolean.opBoolean","COPY",EDGE,{"derivedFrom":makeQuery(id+"F27.opExtrude","SWEPT_EDGE",EDGE,{"disambiguationData":[OSD([sQuery(id+"F26.wireOp",EDGE,"E22.bottom"),sQuery(id+"F26.wireOp",EDGE,"E22.right")])]})});
            var Q18;
            Q18=makeQuery(id+"F27.boolean.opBoolean","COPY",EDGE,{"derivedFrom":makeQuery(id+"F27.opExtrude","SWEPT_EDGE",EDGE,{"disambiguationData":[OSD([sQuery(id+"F26.wireOp",EDGE,"E25.MirrorCS"),sQuery(id+"F26.wireOp",EDGE,"E26.MirrorCS")])]})});
            var Q19;
            Q19=makeQuery(id+"F34.boolean.opBoolean","COPY",EDGE,{"derivedFrom":makeQuery(id+"F34.opExtrude","SWEPT_EDGE",EDGE,{"disambiguationData":[OSD([sQuery(id+"F33.wireOp",EDGE,"E29.top"),sQuery(id+"F33.wireOp",EDGE,"E29.right")])]})});
            var Q20;
            Q20=makeQuery(id+"F34.boolean.opBoolean","COPY",EDGE,{"derivedFrom":makeQuery(id+"F34.opExtrude","SWEPT_EDGE",EDGE,{"disambiguationData":[OSD([sQuery(id+"F33.wireOp",EDGE,"E30.0.1.1"),sQuery(id+"F33.wireOp",EDGE,"E30.0.1.3")])]})});
            var Q21;
            Q21=makeQuery(id+"F34.boolean.opBoolean","COPY",EDGE,{"derivedFrom":makeQuery(id+"F34.opExtrude","SWEPT_EDGE",EDGE,{"disambiguationData":[OSD([sQuery(id+"F33.wireOp",EDGE,"E30.0.2.1"),sQuery(id+"F33.wireOp",EDGE,"E30.0.2.3")])]})});
            var Q22;
            Q22=makeQuery(id+"F34.boolean.opBoolean","COPY",EDGE,{"derivedFrom":makeQuery(id+"F34.opExtrude","SWEPT_EDGE",EDGE,{"disambiguationData":[OSD([sQuery(id+"F33.wireOp",EDGE,"E30.0.3.1"),sQuery(id+"F33.wireOp",EDGE,"E30.0.3.3")])]})});
            var Q23;
            Q23=makeQuery(id+"F27.boolean.opBoolean","COPY",EDGE,{"derivedFrom":makeQuery(id+"F27.opExtrude","SWEPT_EDGE",EDGE,{"disambiguationData":[OSD([sQuery(id+"F26.wireOp",EDGE,"E19.MirrorCS"),sQuery(id+"F26.wireOp",EDGE,"E20.MirrorCS")])]})});
            var Q24;
            Q24=makeQuery(id+"F27.boolean.opBoolean","COPY",EDGE,{"derivedFrom":makeQuery(id+"F27.opExtrude","SWEPT_EDGE",EDGE,{"disambiguationData":[OSD([sQuery(id+"F26.wireOp",EDGE,"E22.top"),sQuery(id+"F26.wireOp",EDGE,"E22.right")])]})});
            var Q25;
            Q25=makeQuery(id+"F27.boolean.opBoolean","COPY",EDGE,{"derivedFrom":makeQuery(id+"F27.opExtrude","SWEPT_EDGE",EDGE,{"disambiguationData":[OSD([sQuery(id+"F26.wireOp",EDGE,"E23.MirrorCS"),sQuery(id+"F26.wireOp",EDGE,"E26.MirrorCS")])]})});
            var Q26;
            Q26=makeQuery(id+"F34.boolean.opBoolean","COPY",EDGE,{"derivedFrom":makeQuery(id+"F34.opExtrude","SWEPT_EDGE",EDGE,{"disambiguationData":[OSD([sQuery(id+"F33.wireOp",EDGE,"E29.top"),sQuery(id+"F33.wireOp",EDGE,"E29.left")])]})});
            var Q27;
            Q27=makeQuery(id+"F34.boolean.opBoolean","COPY",EDGE,{"derivedFrom":makeQuery(id+"F34.opExtrude","SWEPT_EDGE",EDGE,{"disambiguationData":[OSD([sQuery(id+"F33.wireOp",EDGE,"E30.0.1.1"),sQuery(id+"F33.wireOp",EDGE,"E30.0.1.2")])]})});
            var Q28;
            Q28=makeQuery(id+"F34.boolean.opBoolean","COPY",EDGE,{"derivedFrom":makeQuery(id+"F34.opExtrude","SWEPT_EDGE",EDGE,{"disambiguationData":[OSD([sQuery(id+"F33.wireOp",EDGE,"E30.0.2.1"),sQuery(id+"F33.wireOp",EDGE,"E30.0.2.2")])]})});
            var Q29;
            Q29=makeQuery(id+"F34.boolean.opBoolean","COPY",EDGE,{"derivedFrom":makeQuery(id+"F34.opExtrude","SWEPT_EDGE",EDGE,{"disambiguationData":[OSD([sQuery(id+"F33.wireOp",EDGE,"E30.0.3.1"),sQuery(id+"F33.wireOp",EDGE,"E30.0.3.2")])]})});
            var Q30;
            Q30=makeQuery(id+"F27.boolean.opBoolean","COPY",EDGE,{"derivedFrom":makeQuery(id+"F27.opExtrude","SWEPT_EDGE",EDGE,{"disambiguationData":[OSD([sQuery(id+"F26.wireOp",EDGE,"E18.MirrorCS"),sQuery(id+"F26.wireOp",EDGE,"E19.MirrorCS")])]})});
            var Q31;
            Q31=makeQuery(id+"F27.boolean.opBoolean","COPY",EDGE,{"derivedFrom":makeQuery(id+"F27.opExtrude","SWEPT_EDGE",EDGE,{"disambiguationData":[OSD([sQuery(id+"F26.wireOp",EDGE,"E22.top"),sQuery(id+"F26.wireOp",EDGE,"E22.left")])]})});
            fillet(context, id + "F35", {"entities" : qUnion([Q0, Q1, Q2, Q3, Q4, Q5, Q6, Q7, Q8, Q9, Q10, Q11, Q12, Q13, Q14, Q15, Q16, Q17, Q18, Q19, Q20, Q21, Q22, Q23, Q24, Q25, Q26, Q27, Q28, Q29, Q30, Q31]), "radius" : 1 * mm, "tangentPropagation" : true, "allowEdgeOverflow" : false});
        }
        {
            var Q0;
            Q0=makeQuery(id+"F12.opExtrude","CAP_EDGE",EDGE,{"disambiguationData":[OSD([sQuery(id+"F11.wireOp",EDGE,"E5.left")])],"isStart":false});
            var Q1;
            {var subQ0=sQuery(id+"F11.wireOp",EDGE,"E5.bottom");var subQ1=sQuery(id+"F11.wireOp",EDGE,"E5.left");Q1=makeQuery(id+"F20.boolean.opBoolean","SPLIT",EDGE,{"disambiguationData":[TD([makeQuery(id+"F12.opExtrude","SWEPT_FACE",FACE,{"disambiguationData":[OSD([subQ1])]})])],"derivedFrom":makeQuery(id+"F12.opExtrude","CAP_EDGE",EDGE,{"disambiguationData":[OSD([subQ0])],"isStart":false})});}
            var Q2;
            {var subQ0=sQuery(id+"F11.wireOp",EDGE,"E5.bottom");var subQ1=sQuery(id+"F11.wireOp",EDGE,"E5.right");Q2=makeQuery(id+"F20.boolean.opBoolean","SPLIT",EDGE,{"disambiguationData":[TD([makeQuery(id+"F12.opExtrude","SWEPT_FACE",FACE,{"disambiguationData":[OSD([subQ1])]})])],"derivedFrom":makeQuery(id+"F12.opExtrude","CAP_EDGE",EDGE,{"disambiguationData":[OSD([subQ0])],"isStart":false})});}
            var Q3;
            Q3=makeQuery(id+"F12.opExtrude","CAP_EDGE",EDGE,{"disambiguationData":[OSD([sQuery(id+"F11.wireOp",EDGE,"E5.right")])],"isStart":false});
            var Q4;
            {var subQ0=sQuery(id+"F11.wireOp",EDGE,"E5.right");var subQ1=sQuery(id+"F11.wireOp",EDGE,"E5.top");Q4=makeQuery(id+"F20.boolean.opBoolean","SPLIT",EDGE,{"disambiguationData":[TD([makeQuery(id+"F12.opExtrude","SWEPT_FACE",FACE,{"disambiguationData":[OSD([subQ0])]})])],"derivedFrom":makeQuery(id+"F12.opExtrude","CAP_EDGE",EDGE,{"disambiguationData":[OSD([subQ1])],"isStart":false})});}
            var Q5;
            {var subQ0=sQuery(id+"F11.wireOp",EDGE,"E5.left");var subQ1=sQuery(id+"F11.wireOp",EDGE,"E5.top");Q5=makeQuery(id+"F20.boolean.opBoolean","SPLIT",EDGE,{"disambiguationData":[TD([makeQuery(id+"F12.opExtrude","SWEPT_FACE",FACE,{"disambiguationData":[OSD([subQ0])]})])],"derivedFrom":makeQuery(id+"F12.opExtrude","CAP_EDGE",EDGE,{"disambiguationData":[OSD([subQ1])],"isStart":false})});}
            chamfer(context, id + "F36", {"entities" : qUnion([Q0, Q1, Q2, Q3, Q4, Q5]), "width" : 0.5 * mm, "tangentPropagation" : true});
        }
        {
            var Q0;
            Q0=makeQuery(id+"F2.opExtrude","CAP_EDGE",EDGE,{"disambiguationData":[OSD([sQuery(id+"F0.wireOp",EDGE,"E1.3")])],"isStart":false});
            chamfer(context, id + "F37", {"entities" : qUnion([Q0]), "width" : 0.5 * mm, "tangentPropagation" : true});
        }
    });
